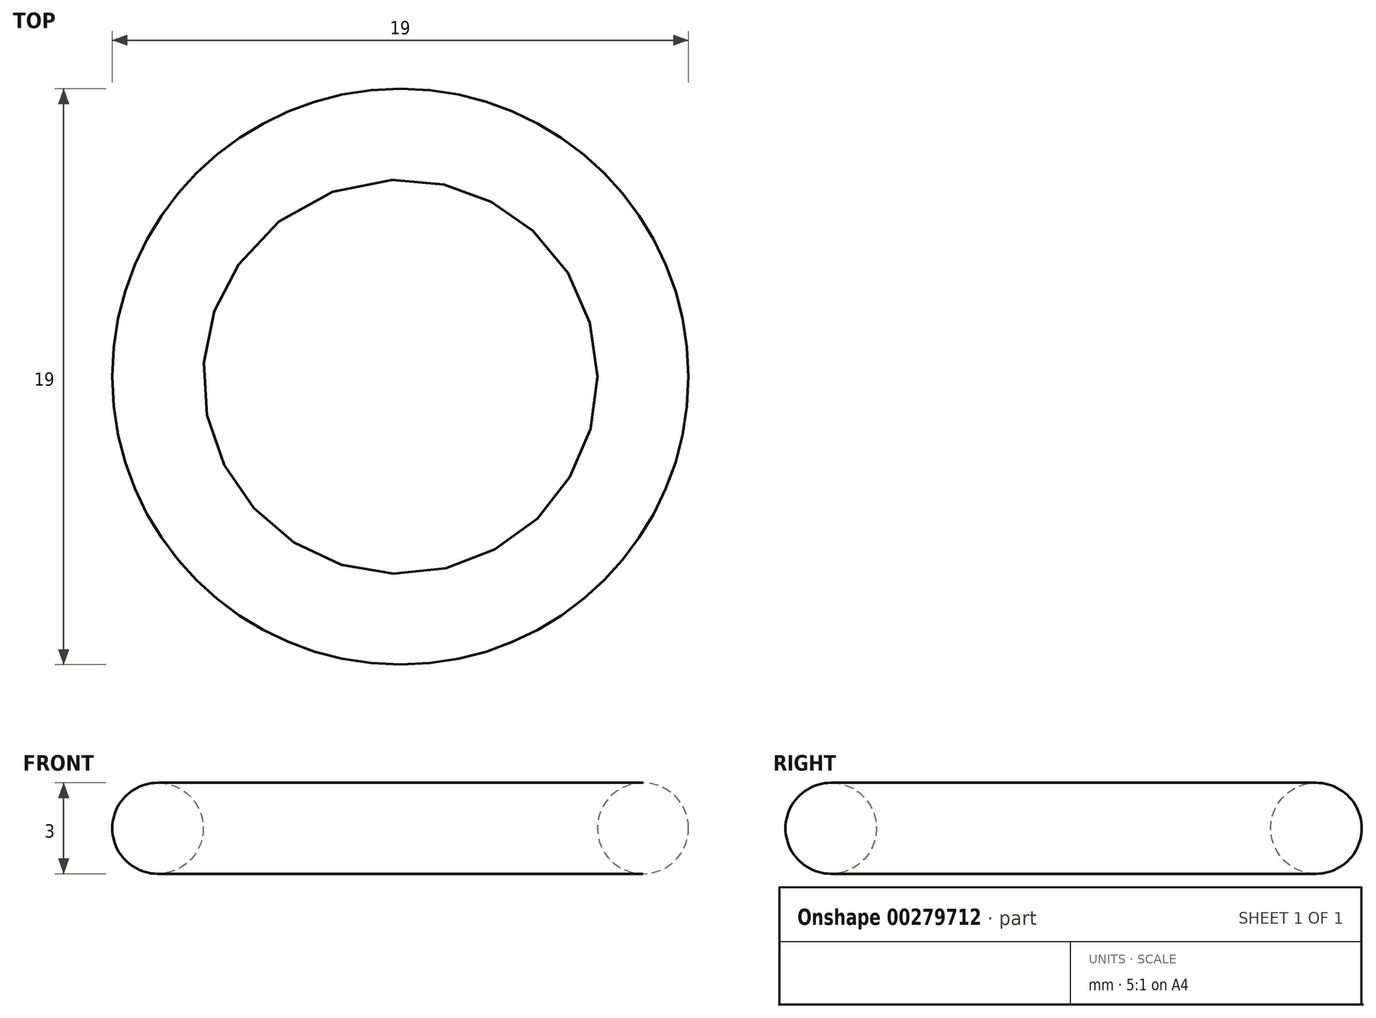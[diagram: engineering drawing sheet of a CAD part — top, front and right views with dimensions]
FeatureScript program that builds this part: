
annotation { "Feature Type Name" : "Feature", "Feature Type Description" : "" }
export const myFeature = defineFeature(function(context is Context, id is Id, definition is map)
    precondition{}
    {
        {
            var Q0;
            Q0=qCreatedBy(makeId("Front.planeOp"),FACE);
            var sketch = newSketch(context, id + "F0", { "sketchPlane" : qUnion([Q0])});
            skCircle(sketch, "E0", {"center": v(-8, 0) * mm, "radius": 1.5 * mm});
            skLineSegment(sketch, "E1", {"start": v(0, 5.3) * mm, "end": v(0, -6.5) * mm, "construction": true});
            skSolve(sketch);
        }
        {
            var Q0;
            Q0=makeQuery(id+"F0.imprint","IMPRINT",FACE,{"disambiguationData":[TD([[makeQuery(id+"F0.imprint","IMPRINT",EDGE,{"derivedFrom":sQuery(id+"F0.wireOp",EDGE,"E0")}),1.0]])]});
            var Q1;
            Q1=sQuery(id+"F0.wireOp",EDGE,"E1");
            revolve(context, id + "F1", {"entities" : qUnion([Q0]), "axis" : qUnion([Q1]), "revolveType" : RevolveType.FULL});
        }
    });
